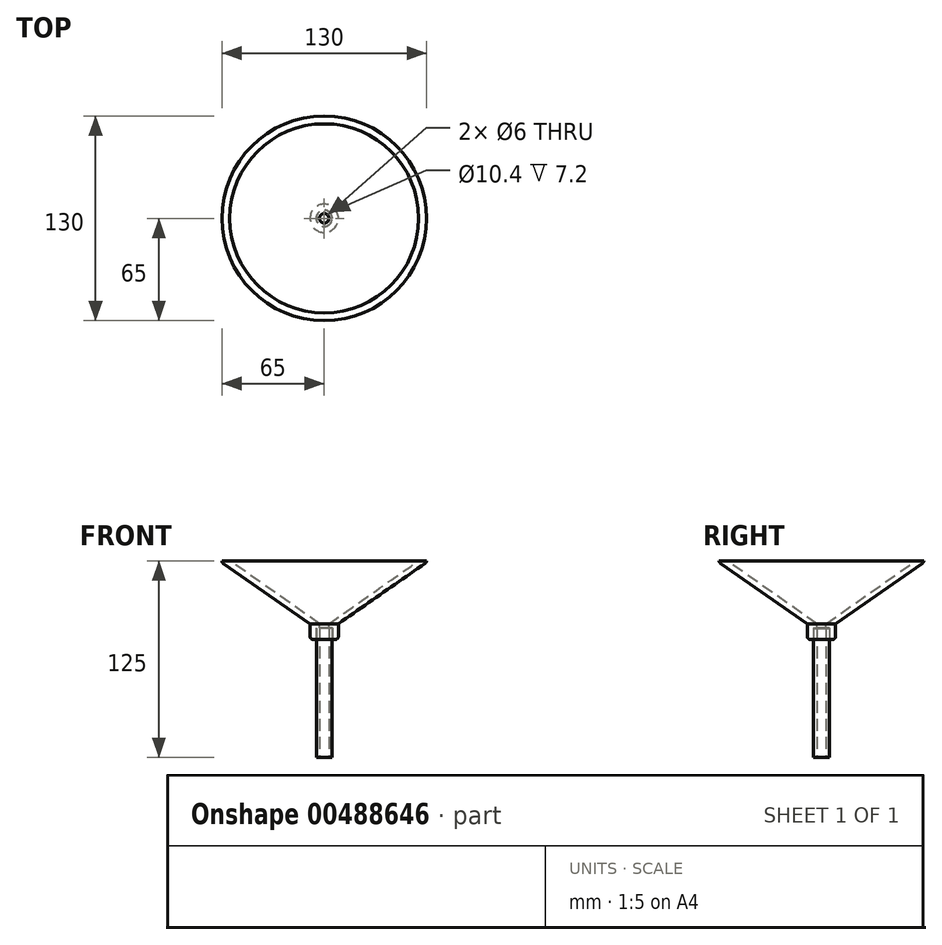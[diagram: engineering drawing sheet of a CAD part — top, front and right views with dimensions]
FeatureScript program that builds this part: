
annotation { "Feature Type Name" : "Feature", "Feature Type Description" : "" }
export const myFeature = defineFeature(function(context is Context, id is Id, definition is map)
    precondition{}
    {
        {
            var Q0;
            Q0=qCreatedBy(makeId("Top.planeOp"),FACE);
            var sketch = newSketch(context, id + "F0", { "sketchPlane" : qUnion([Q0])});
            skCircle(sketch, "E0", {"center": v(0, 0) * mm, "radius": 65 * mm});
            skCircle(sketch, "E1", {"center": v(0, 0) * mm, "radius": 60 * mm});
            skSolve(sketch);
        }
        {
            var Q0;
            Q0=makeQuery(id+"F0.imprint","IMPRINT",FACE,{"disambiguationData":[TD([[makeQuery(id+"F0.imprint","IMPRINT",EDGE,{"derivedFrom":sQuery(id+"F0.wireOp",EDGE,"E0")}),1.0]])]});
            var Q1;
            Q1=makeQuery(id+"F0.imprint","IMPRINT",FACE,{"disambiguationData":[TD([[makeQuery(id+"F0.imprint","IMPRINT",EDGE,{"derivedFrom":sQuery(id+"F0.wireOp",EDGE,"E1")}),1.0]])]});
            extrude(context, id + "F1", {"entities" : qUnion([Q0, Q1]), "oppositeDirection" : true, "offsetDistance" : 25 * mm, "depth" : 40 * mm});
        }
        {
            var Q0;
            Q0=makeQuery(id+"F1.opExtrude","CAP_FACE",FACE,{"disambiguationData":[OSD([sQuery(id+"F0.wireOp",EDGE,"E0")])],"isStart":false});
            var sketch = newSketch(context, id + "F2", { "sketchPlane" : qUnion([Q0])});
            skCircle(sketch, "E2", {"center": v(0, 0) * mm, "radius": 5 * mm});
            skCircle(sketch, "E3", {"center": v(0, 0) * mm, "radius": 3 * mm});
            skSolve(sketch);
        }
        {
            var Q1;
            Q1=makeQuery(id+"F0.imprint","IMPRINT",FACE,{"disambiguationData":[TD([[makeQuery(id+"F0.imprint","IMPRINT",EDGE,{"derivedFrom":sQuery(id+"F0.wireOp",EDGE,"E1")}),1.0]])]});
            var Q2;
            Q2=makeQuery(id+"F2.imprint","IMPRINT",FACE,{"disambiguationData":[TD([[makeQuery(id+"F2.imprint","IMPRINT",EDGE,{"derivedFrom":sQuery(id+"F2.wireOp",EDGE,"E3")}),1.0]])]});
            loft(context, id + "F3", {"operationType" : NewBodyOperationType.REMOVE, "sheetProfilesArray" : [{ "sheetProfileEntities" : qUnion([Q1]) }, { "sheetProfileEntities" : qUnion([Q2]) }]});
        }
        {
            var Q0;
            Q0=makeQuery(id+"F1.opExtrude","CAP_EDGE",EDGE,{"disambiguationData":[OSD([sQuery(id+"F0.wireOp",EDGE,"E0")])],"isStart":false});
            chamfer(context, id + "F4", {"entities" : qUnion([Q0]), "chamferType" : ChamferType.TWO_OFFSETS, "width1" : 39 * mm, "oppositeDirection" : false, "width2" : 56 * mm, "tangentPropagation" : true});
        }
        {
            var Q0;
            Q0=makeQuery(id+"F1.opExtrude","CAP_FACE",FACE,{"disambiguationData":[OSD([sQuery(id+"F0.wireOp",EDGE,"E0")])],"isStart":false});
            extrude(context, id + "F5", {"entities" : qUnion([Q0]), "operationType" : NewBodyOperationType.ADD, "depth" : 10 * mm, "offsetDistance" : 25 * mm});
        }
        {
            var Q0;
            Q0=makeQuery(id+"F5.opExtrude","CAP_EDGE",EDGE,{"disambiguationData":[OSD([sQuery(id+"F0.wireOp",EDGE,"E0")])],"isStart":false});
            var Q1;
            {var subQ0=sQuery(id+"F0.wireOp",EDGE,"E0");Q1=makeQuery(id+"F4.opChamfer","BLEND_EDGE",EDGE,{"blendedFrom":[makeQuery(id+"F1.opExtrude","CAP_EDGE",EDGE,{"disambiguationData":[OSD([subQ0])],"isStart":false}),makeQuery(id+"F1.opExtrude","SWEPT_FACE",FACE,{"disambiguationData":[OSD([subQ0])]})],"blendedInto":[makeQuery(id+"F1.opExtrude","SWEPT_FACE",FACE,{"disambiguationData":[OSD([subQ0])]})]});}
            fillet(context, id + "F6", {"entities" : qUnion([Q0, Q1]), "radius" : 2 * mm, "tangentPropagation" : true, "allowEdgeOverflow" : false});
        }
        {
            var Q0;
            Q0=qCreatedBy(makeId("Top.planeOp"),FACE);
            cPlane(context, id + "F7", {"entities" : qUnion([Q0]), "cplaneType" : CPlaneType.OFFSET, "offset" : 85 * mm, "oppositeDirection" : true, "width" : 150 * mm, "height" : 150 * mm});
        }
        {
            var Q0;
            Q0=qCreatedBy(id+"F7.planeOp",FACE);
            var sketch = newSketch(context, id + "F8", { "sketchPlane" : qUnion([Q0])});
            skCircle(sketch, "E4", {"center": v(0, 0) * mm, "radius": 5 * mm});
            skCircle(sketch, "E5", {"center": v(0, 0) * mm, "radius": 3 * mm});
            skSolve(sketch);
        }
        {
            var Q0;
            Q0=makeQuery(id+"F8.imprint","IMPRINT",FACE,{"disambiguationData":[TD([[makeQuery(id+"F8.imprint","IMPRINT",EDGE,{"derivedFrom":sQuery(id+"F8.wireOp",EDGE,"E4")}),1.0]])]});
            extrude(context, id + "F9", {"entities" : qUnion([Q0]), "depth" : 42 * mm, "offsetDistance" : 25 * mm});
        }
        {
            var Q0;
            Q0=makeQuery(id+"F9.opExtrude","SWEPT_BODY",BODY,{"disambiguationData":[OSD([sQuery(id+"F8.wireOp",EDGE,"E4"),sQuery(id+"F8.wireOp",EDGE,"E5")])]});
            var Q1;
            Q1=makeQuery(id+"F1.opExtrude","SWEPT_BODY",BODY,{"disambiguationData":[OSD([sQuery(id+"F0.wireOp",EDGE,"E0")])]});
            booleanBodies(context, id + "F10", {"operationType" : BooleanOperationType.SUBTRACTION, "tools" : qUnion([Q0]), "targets" : qUnion([Q1]), "offset" : true, "offsetAll" : true, "offsetDistance" : 0.2 * mm, "keepTools" : true});
        }
        {
            var Q0;
            Q0=makeQuery(id+"F9.opExtrude","CAP_FACE",FACE,{"disambiguationData":[OSD([sQuery(id+"F8.wireOp",EDGE,"E4"),sQuery(id+"F8.wireOp",EDGE,"E5")])],"isStart":true});
            extrude(context, id + "F11", {"entities" : qUnion([Q0]), "operationType" : NewBodyOperationType.ADD, "depth" : 40 * mm, "offsetDistance" : 25 * mm});
        }
    });
